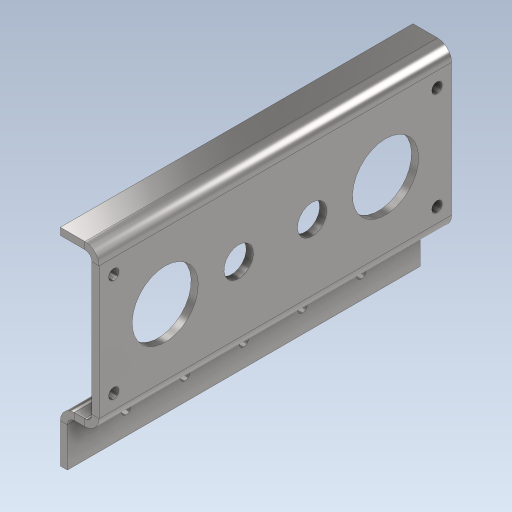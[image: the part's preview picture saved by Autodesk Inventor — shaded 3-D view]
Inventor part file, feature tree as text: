
AUTODESK INVENTOR PART (.ipt)
format: ipt  version: 2023 (Build 270158000, 158)  size: 232,960 bytes
history: native  units: in
note: dims shown in document units (in); Inventor stores cm internally (conversion verified against a paired STEP export)
features: sheet_metal_op x7, sketch x5, other x3, hole x2, projected_geometry x1
ambient origin geometry x8: Origin, YZ Plane, XZ Plane, XY Plane, X Axis, Y Axis, Z Axis, Center Point
bodies: Body1 (feature_tree)
feature tree (18):
  sheet_metal_op  "Face2"
  sheet_metal_op  "Flange1"
  sheet_metal_op  "Flange2"
  hole  "Hole2"  [1 undecoded]
  hole  "Hole1"  [1 undecoded]
  sketch  "Sketch1"  dims[d0=2.25in d1=6.0in]
  other  "Plate2"
  sketch  "Sketch2"  dims[d2=1.25in d3=1.25in]
  other  "Plate3"
  sheet_metal_op  "Bend1"
  sheet_metal_op  "Corner1"
  sketch  "Sketch3"  dims[d4=1.25in]
  projected_geometry  "Projected Loop1"
  sketch  "Sketch4"  dims[d6=1.125in]
  other  "Plate4"
  sheet_metal_op  "Bend2"
  sheet_metal_op  "Corner2"
  sketch  "Sketch5"  dims[d7=0.5in d8=1.125in d10=0.12in d11=0.177in d12=5.5in d13=1.75in d14=0.5in d15=6.0in d16=0.5in d17=6.0in d18=0.12in d19=0.06in d20=0.24in d21=0.12in d22=0.6583in d23=90.0deg d24=0.12in d25=0.48in d26=0.12in d27=0.12in d28=1.0in d29=1.9685in d31=1.0in d32=0.3937in d34=1.0in d36=0.1628in d37=5.0in d38=0.375in d39=0.25in d40=0.5635in d41=0.12in d42=0.8108in d43=0.12in d44=0.06in d45=0.24in d46=0.12in d47=0.7874in d48=90.0deg d49=0.12in d50=0.48in d51=0.12in d52=0.12in d53=1.0in d54=0.3937in d55=1.9685in d57=1.0in d58=0.3937in d60=1.0in d62=0.1628in d63=0.394in d64=0.375in d65=0.25in d66=0.5635in d67=1.0in d68=0.8108in]
note: 2 required parameter values undecoded (feature->parameter linkage not recoverable at this tier; creation-order binding heuristic only, values carry confidence <= 0.55)
